# Revit family: Reception-05-With_Transaction-Layout-Teknion-2016
name_source: partatom
category: Furniture Systems
revit_build: Autodesk Revit Architecture 2016 (Build: 20150220_1215(x64)
units: mm (PartAtom-declared; Revit-internal decimal feet)

## family parameters
Always vertical = Yes
Cut with Voids When Loaded = No
OmniClass Number = 23.40.20.00
OmniClass Title = General Furniture and Specialties
Part Type = Normal
Room Calculation Point = No
Round Connector Dimension = Use Diameter
Shared = Yes
Work Plane-Based = No

## types (3) — shared parameters
Assembly Code = E2020200
Description = 6'-9" x 10'-3" Overall
Manufacturer = Teknion
Manufacturer Fax = 416.661.4586
Model = Reception 06 - With Transaction Layout
Product Line = Reception
Product Page URL = https://www.teknionplanningtool.com
Series = Reception
Sustainability Data = https://www.teknion.com
URL = www.teknion.com
Unit Weight URL = http://www.teknion.com
Warranty = http://www.teknion.com

## per-type parameters (varying)
| type | Center | Closed | Edge offset | LeftorRight | Open |
| Left/Right Transaction Counter with Open Waterfall Edge | No | No | 3 " | Yes | Yes |
| Left/Right Transaction Counter with Closed Waterfall Edge | No | Yes | 3 " | Yes | No |
| Center Transaction Counter with Closed Waterfall Edge | Yes | Yes | 0 " | No | No |

## geometry (parser evidence)
native form markers: Blend x20, Sweep x14
no freeform markers — native parametric forms only
